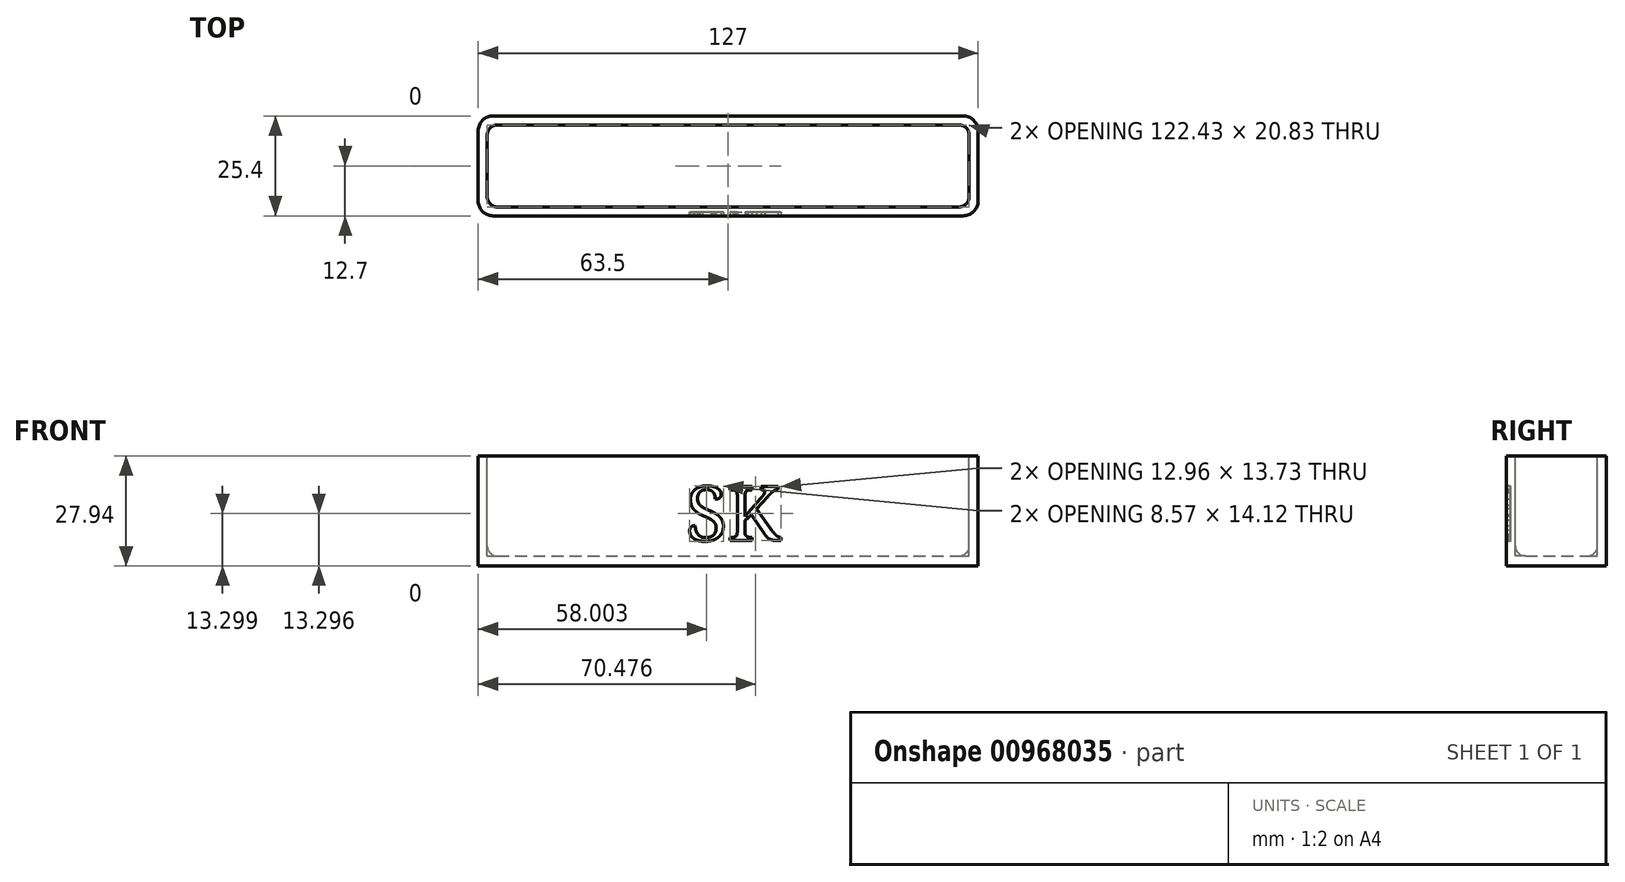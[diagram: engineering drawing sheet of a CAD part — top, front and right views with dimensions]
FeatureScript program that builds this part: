
annotation { "Feature Type Name" : "Feature", "Feature Type Description" : "" }
export const myFeature = defineFeature(function(context is Context, id is Id, definition is map)
    precondition{}
    {
        {
            var Q0;
            Q0=qCreatedBy(makeId("Top.planeOp"),FACE);
            var sketch = newSketch(context, id + "F0", { "sketchPlane" : qUnion([Q0])});
            skLineSegment(sketch, "E0.bottom", {"start": v(63.5, -12.7) * mm, "end": v(-63.5, -12.7) * mm});
            skLineSegment(sketch, "E0.top", {"start": v(63.5, 12.7) * mm, "end": v(-63.5, 12.7) * mm});
            skLineSegment(sketch, "E0.left", {"start": v(63.5, -12.7) * mm, "end": v(63.5, 12.7) * mm});
            skLineSegment(sketch, "E0.right", {"start": v(-63.5, -12.7) * mm, "end": v(-63.5, 12.7) * mm});
            skPoint(sketch, "E0.middle", {"position": v(0, 0) * mm});
            skSolve(sketch);
        }
        {
            var Q0;
            Q0=makeQuery(id+"F0.imprint","IMPRINT",FACE,{"disambiguationData":[TD([[makeQuery(id+"F0.imprint","IMPRINT",EDGE,{"derivedFrom":sQuery(id+"F0.wireOp",EDGE,"E0.bottom")}),-1.0]])]});
            extrude(context, id + "F1", {"entities" : qUnion([Q0]), "depth" : 27.94 * mm, "offsetDistance" : 25.4 * mm});
        }
        {
            var Q0;
            Q0=makeQuery(id+"F1.opExtrude","CAP_FACE",FACE,{"disambiguationData":[OSD([sQuery(id+"F0.wireOp",EDGE,"E0.bottom"),sQuery(id+"F0.wireOp",EDGE,"E0.top"),sQuery(id+"F0.wireOp",EDGE,"E0.left"),sQuery(id+"F0.wireOp",EDGE,"E0.right")])],"isStart":false});
            var sketch = newSketch(context, id + "F2", { "sketchPlane" : qUnion([Q0])});
            skLineSegment(sketch, "E1.0", {"start": v(61.21, -10.41) * mm, "end": v(61.21, 10.41) * mm});
            skLineSegment(sketch, "E1.1", {"start": v(-61.21, -10.41) * mm, "end": v(61.21, -10.41) * mm});
            skLineSegment(sketch, "E1.2", {"start": v(-61.21, 10.41) * mm, "end": v(-61.21, -10.41) * mm});
            skLineSegment(sketch, "E1.3", {"start": v(61.21, 10.41) * mm, "end": v(-61.21, 10.41) * mm});
            skSolve(sketch);
        }
        {
            var Q0;
            Q0=makeQuery(id+"F2.imprint","IMPRINT",FACE,{"disambiguationData":[TD([[makeQuery(id+"F2.imprint","IMPRINT",EDGE,{"derivedFrom":sQuery(id+"F2.wireOp",EDGE,"E1.0")}),1.0]])]});
            extrude(context, id + "F3", {"entities" : qUnion([Q0]), "operationType" : NewBodyOperationType.REMOVE, "oppositeDirection" : true, "depth" : 25.4 * mm, "offsetDistance" : 25.4 * mm});
        }
        {
            var Q0;
            Q0=makeQuery(id+"F3.boolean.opBoolean","COPY",FACE,{"derivedFrom":makeQuery(id+"F3.opExtrude","CAP_FACE",FACE,{"disambiguationData":[OSD([sQuery(id+"F2.wireOp",EDGE,"E1.0"),sQuery(id+"F2.wireOp",EDGE,"E1.1"),sQuery(id+"F2.wireOp",EDGE,"E1.2"),sQuery(id+"F2.wireOp",EDGE,"E1.3")])],"isStart":false})});
            var Q1;
            Q1=makeQuery(id+"F3.boolean.opBoolean","COPY",EDGE,{"derivedFrom":makeQuery(id+"F3.opExtrude","SWEPT_EDGE",EDGE,{"disambiguationData":[OSD([sQuery(id+"F2.wireOp",EDGE,"E1.2"),sQuery(id+"F2.wireOp",EDGE,"E1.3")])]})});
            var Q2;
            Q2=makeQuery(id+"F3.boolean.opBoolean","COPY",EDGE,{"derivedFrom":makeQuery(id+"F3.opExtrude","SWEPT_EDGE",EDGE,{"disambiguationData":[OSD([sQuery(id+"F2.wireOp",EDGE,"E1.0"),sQuery(id+"F2.wireOp",EDGE,"E1.3")])]})});
            var Q3;
            Q3=makeQuery(id+"F3.boolean.opBoolean","COPY",EDGE,{"derivedFrom":makeQuery(id+"F3.opExtrude","SWEPT_EDGE",EDGE,{"disambiguationData":[OSD([sQuery(id+"F2.wireOp",EDGE,"E1.0"),sQuery(id+"F2.wireOp",EDGE,"E1.1")])]})});
            var Q4;
            Q4=makeQuery(id+"F3.boolean.opBoolean","COPY",EDGE,{"derivedFrom":makeQuery(id+"F3.opExtrude","SWEPT_EDGE",EDGE,{"disambiguationData":[OSD([sQuery(id+"F2.wireOp",EDGE,"E1.1"),sQuery(id+"F2.wireOp",EDGE,"E1.2")])]})});
            fillet(context, id + "F4", {"entities" : qUnion([Q0, Q1, Q2, Q3, Q4]), "radius" : 2.54 * mm, "tangentPropagation" : true, "allowEdgeOverflow" : false});
        }
        {
            var Q0;
            Q0=makeQuery(id+"F1.opExtrude","SWEPT_EDGE",EDGE,{"disambiguationData":[OSD([sQuery(id+"F0.wireOp",EDGE,"E0.bottom"),sQuery(id+"F0.wireOp",EDGE,"E0.right")])]});
            var Q1;
            Q1=makeQuery(id+"F1.opExtrude","SWEPT_EDGE",EDGE,{"disambiguationData":[OSD([sQuery(id+"F0.wireOp",EDGE,"E0.top"),sQuery(id+"F0.wireOp",EDGE,"E0.right")])]});
            var Q2;
            Q2=makeQuery(id+"F1.opExtrude","SWEPT_EDGE",EDGE,{"disambiguationData":[OSD([sQuery(id+"F0.wireOp",EDGE,"E0.top"),sQuery(id+"F0.wireOp",EDGE,"E0.left")])]});
            var Q3;
            Q3=makeQuery(id+"F1.opExtrude","SWEPT_EDGE",EDGE,{"disambiguationData":[OSD([sQuery(id+"F0.wireOp",EDGE,"E0.bottom"),sQuery(id+"F0.wireOp",EDGE,"E0.left")])]});
            fillet(context, id + "F5", {"entities" : qUnion([Q0, Q1, Q2, Q3]), "radius" : 3.8 * mm, "tangentPropagation" : true, "allowEdgeOverflow" : false});
        }
        {
            var Q0;
            Q0=makeQuery(id+"F1.opExtrude","SWEPT_FACE",FACE,{"disambiguationData":[OSD([sQuery(id+"F0.wireOp",EDGE,"E0.bottom")])]});
            var sketch = newSketch(context, id + "F6", { "sketchPlane" : qUnion([Q0])});
            skLineSegment(sketch, "E2", {"start": v(0, 27.94) * mm, "end": v(0, 0) * mm, "construction": true});
            skText(sketch, "E3", { "text": "SK", "fontName": "NotoSerif-Regular.ttf"});
            const initialGuessF6  = {"E3": [-0.0107, 0.00643, 1, 0, 0.01385]};
            skSetInitialGuess(sketch, initialGuessF6);
            skSolve(sketch);
        }
        {
            var Q0;
            Q0=qSketchRegion(id+"F6",true);
            var Q1;
            Q1 = qSketchRegion(id + "F1vEiFf60ZHkyaG_1", true);
            extrude(context, id + "F7", {"entities" : qUnion([Q0, Q1]), "operationType" : NewBodyOperationType.REMOVE, "oppositeDirection" : true, "depth" : 1.02 * mm, "offsetDistance" : 25.4 * mm});
        }
    });
